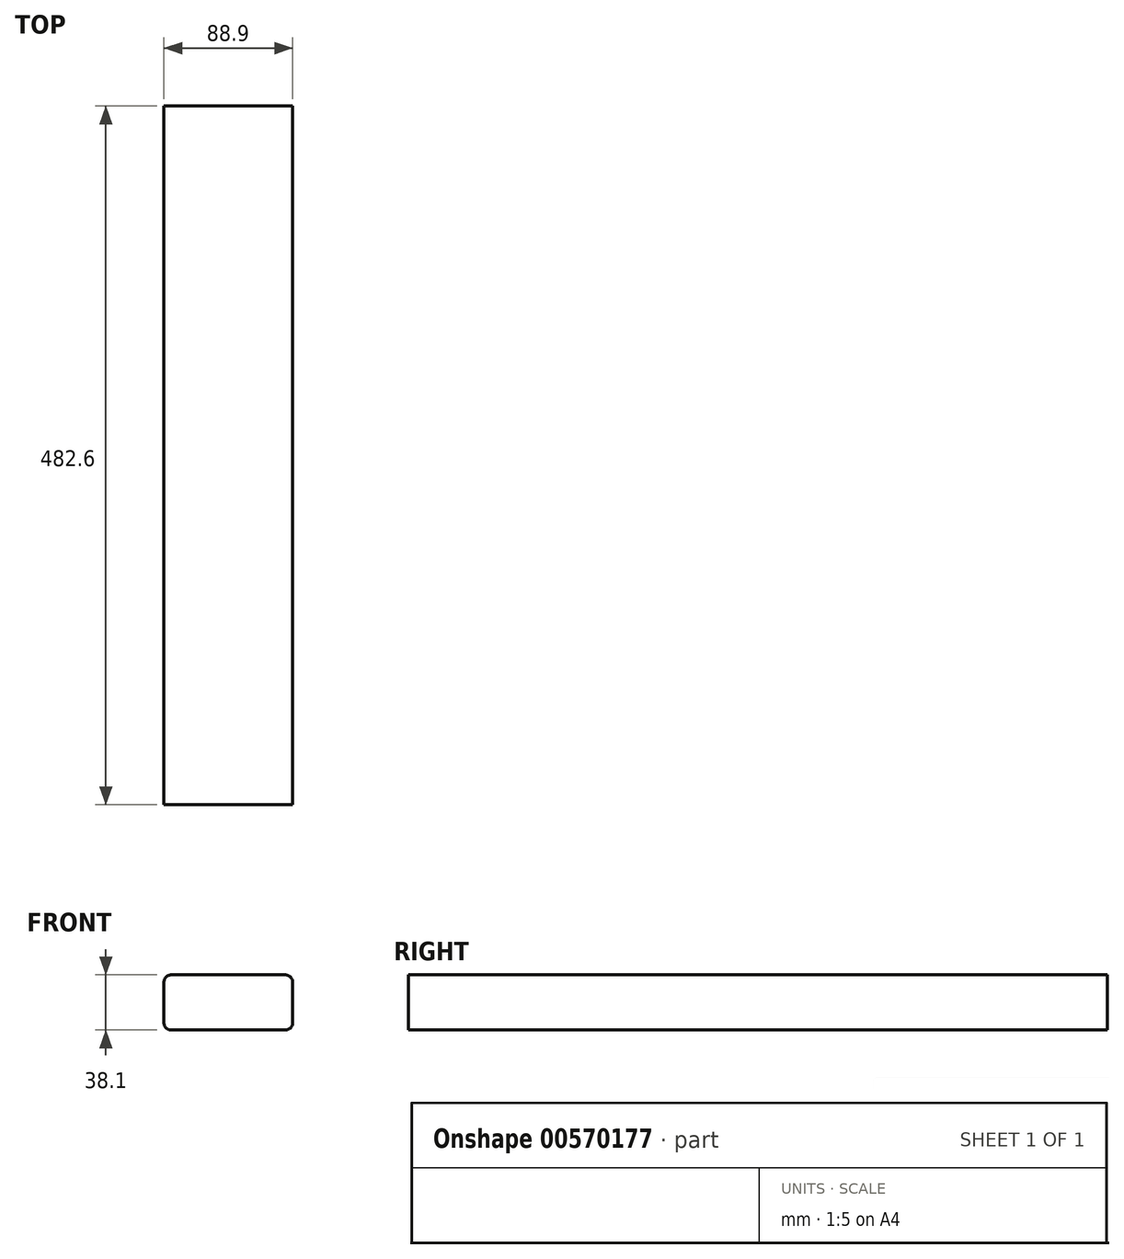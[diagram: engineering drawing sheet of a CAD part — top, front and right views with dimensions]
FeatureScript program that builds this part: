
annotation { "Feature Type Name" : "Feature", "Feature Type Description" : "" }
export const myFeature = defineFeature(function(context is Context, id is Id, definition is map)
    precondition{}
    {
        {
            var Q0;
            Q0=qCreatedBy(makeId("Front.planeOp"),FACE);
            var sketch = newSketch(context, id + "F0", { "sketchPlane" : qUnion([Q0])});
            skLineSegment(sketch, "E0.bottom", {"start": v(0, 0) * mm, "end": v(88.9, 0) * mm});
            skLineSegment(sketch, "E0.top", {"start": v(0, 38.1) * mm, "end": v(88.9, 38.1) * mm});
            skLineSegment(sketch, "E0.left", {"start": v(0, 0) * mm, "end": v(0, 38.1) * mm});
            skLineSegment(sketch, "E0.right", {"start": v(88.9, 0) * mm, "end": v(88.9, 38.1) * mm});
            skSolve(sketch);
        }
        {
            var Q0;
            Q0 = qSketchRegion(id + "F0", true);
            extrude(context, id + "F1", {"entities" : qUnion([Q0]), "depth" : 482.6 * mm, "offsetDistance" : 25.4 * mm});
        }
        {
            var Q0;
            Q0=makeQuery(id+"F1.opExtrude","SWEPT_EDGE",EDGE,{"disambiguationData":[OSD([sQuery(id+"F0.wireOp",EDGE,"E0.top"),sQuery(id+"F0.wireOp",EDGE,"E0.left")])]});
            var Q1;
            Q1=makeQuery(id+"F1.opExtrude","SWEPT_EDGE",EDGE,{"disambiguationData":[OSD([sQuery(id+"F0.wireOp",EDGE,"E0.bottom"),sQuery(id+"F0.wireOp",EDGE,"E0.left")])]});
            var Q2;
            Q2=makeQuery(id+"F1.opExtrude","SWEPT_EDGE",EDGE,{"disambiguationData":[OSD([sQuery(id+"F0.wireOp",EDGE,"E0.bottom"),sQuery(id+"F0.wireOp",EDGE,"E0.right")])]});
            var Q3;
            Q3=makeQuery(id+"F1.opExtrude","SWEPT_EDGE",EDGE,{"disambiguationData":[OSD([sQuery(id+"F0.wireOp",EDGE,"E0.top"),sQuery(id+"F0.wireOp",EDGE,"E0.right")])]});
            fillet(context, id + "F2", {"entities" : qUnion([Q0, Q1, Q2, Q3]), "radius" : 5.08 * mm, "tangentPropagation" : true, "allowEdgeOverflow" : false});
        }
    });
